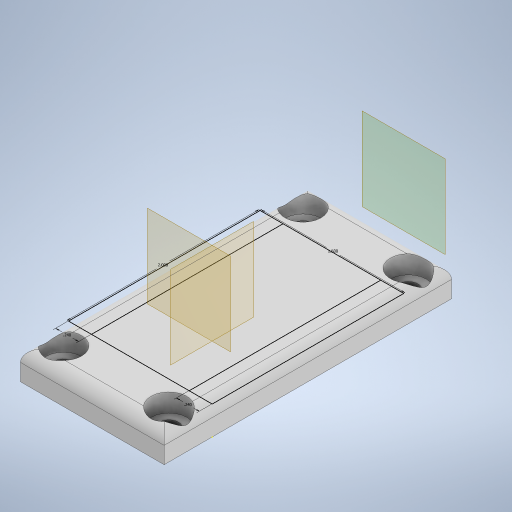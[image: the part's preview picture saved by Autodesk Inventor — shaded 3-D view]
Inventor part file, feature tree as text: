
AUTODESK INVENTOR PART (.ipt)
format: ipt  version: 2024.1 (Build 281209000, 209)  size: 348,672 bytes
history: native  units: in
note: dims shown in document units (in); Inventor stores cm internally (conversion verified against a paired STEP export)
features: sketch x6, extrude x4, plane x3, hole x2, projected_geometry x2, fillet x1
ambient origin geometry x8: Origin, YZ Plane, XZ Plane, XY Plane, X Axis, Y Axis, Z Axis, Center Point
bodies: Solid1 (feature_tree)
feature tree (18):
  extrude  "Extrusion2"  Depth=2.0in
  plane  "Work Plane1"
  plane  "Work Plane2"
  plane  "Work Plane3"
  extrude  "Extrusion3"  Depth=0.24in
  extrude  "Extrusion4"  Depth=0.5in TaperAngle=0.0deg
  extrude  "Extrusion5"  Depth=0.62in
  sketch  "Sketch6"  dims[d18=0.5in d19=0.0in d20=0.62in]
  hole  "Hole2"  [1 undecoded]
  hole  "Hole3"  [1 undecoded]
  fillet  "Fillet1"  Radius=0.1in
  sketch  "Sketch3"  dims[d0=1.5in d1=2.0in]
  projected_geometry  "Projected Loop1"
  sketch  "Sketch4"  dims[d2=0.24in d3=0.24in]
  projected_geometry  "Projected Loop2"
  sketch  "Sketch5"  dims[d6=0.2in d7=0.0in d16=0.5in d17=0.0in]
  sketch  "Sketch7"  dims[d21=2.02in d22=0.5in]
  sketch  "Sketch8"  dims[d23=1.75in d24=0.5in d25=0.1in d26=0.0in d27=0.2in d28=0.25in d29=0.2in d30=0.25in d31=0.2in d32=0.25in d33=0.2in d34=0.1495in d35=0.75in d36=0.375in d37=0.25in d38=0.5635in d39=1.0in d40=0.8108in d41=0.201in d42=0.38in d43=0.375in d44=0.19in d45=0.5635in d46=1.0in d47=0.8108in d48=0.125in]
note: 2 required parameter values undecoded (feature->parameter linkage not recoverable at this tier; creation-order binding heuristic only, values carry confidence <= 0.55)
